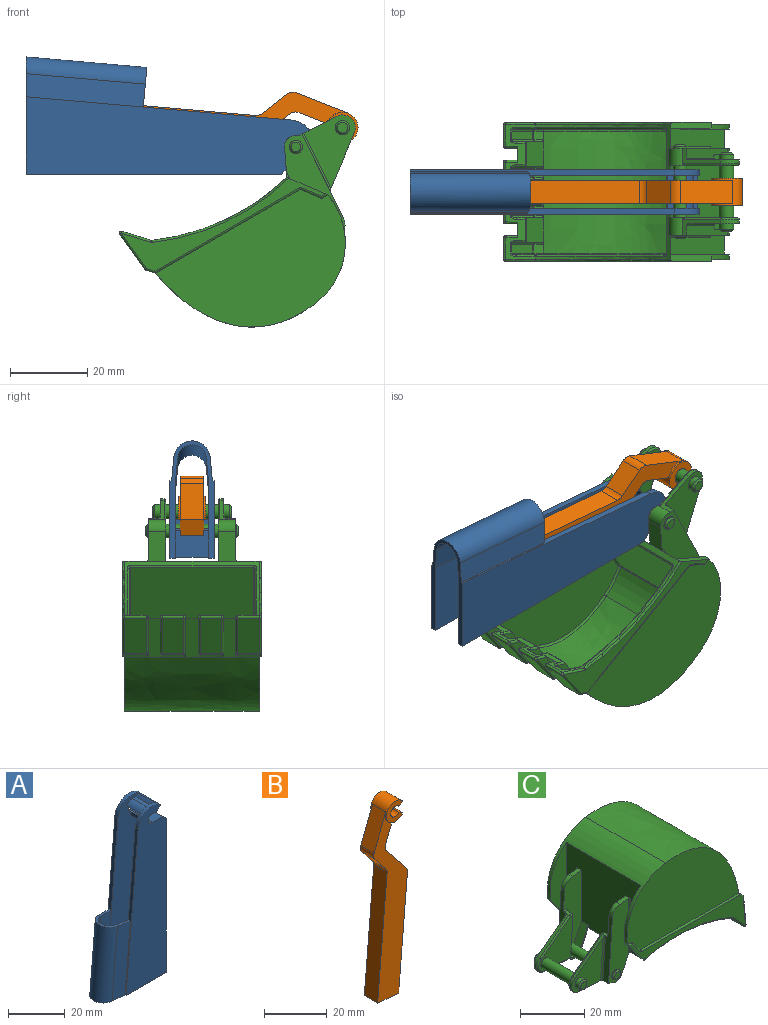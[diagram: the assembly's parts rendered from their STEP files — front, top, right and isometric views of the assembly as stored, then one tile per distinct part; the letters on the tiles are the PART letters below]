
ASSEMBLY  parts=3 mates=3
PART A: 29 faces, bbox 30.3x11.5x75.4 mm
  f0: plane 68.6x6mm, normal (-1,0,0.09), area 72.7mm2, adj f5,f6,f12,f14,f22,f25
  f1: plane 68.6x6mm, normal (-1,0,0.09), area 72.7mm2, adj f6,f12,f13,f19,f22,f24
  f2: cylinder r=1.9mm len=11.5mm, axis (0,1,0), area 30.8mm2, adj f5,f9,f10,f13,f14,f19,f20,f21
  f3: cylinder r=3.4mm len=8.5mm, axis (0,1,0), area 29.8mm2, adj f14,f17,f19,f20
  f4: plane 66.22x1.5mm, normal (1,0,0), area 99.3mm2, adj f5,f6,f8,f14
  f5: plane 75x20mm, normal (0,-1,0), area 1199.2mm2, adj f0,f2,f4,f6,f8,f9,f10,f11
  f6: plane 30.33x11.5mm, normal (0,0,-1), area 84.6mm2, adj f0,f1,f4,f5,f7,f13,f14,f19
  f7: plane 66.22x1.5mm, normal (1,0,0), area 99.3mm2, adj f6,f8,f13,f19
  f8: plane 11.5x1.77mm, normal (0.71,0,0.71), area 25.5mm2, adj f4,f5,f7,f9,f13,f14,f15,f19
  f9: plane 11.5x5.25mm, normal (0,0,1), area 60.3mm2, adj f2,f5,f8,f13
  f10: plane 11.5x2.5mm, normal (0,0,-1), area 28.7mm2, adj f2,f5,f11,f13
  f11: plane 11.5x1.77mm, normal (0.71,0,-0.71), area 28.8mm2, adj f5,f10,f12,f13
  f12: cylinder r=7.01mm len=11.5mm, axis (0,1,0), area 58.1mm2, adj f0,f1,f5,f11,f13,f14,f18,f19
  f13: plane 75x20mm, normal (0,1,0), area 1199.2mm2, adj f1,f2,f6,f7,f8,f9,f10,f11
  f14: plane 75x20mm, normal (0,1,0), area 1179.4mm2, adj f0,f2,f3,f4,f6,f8,f12,f15
  f15: plane 8.5x6.75mm, normal (0,0,-1), area 57.3mm2, adj f8,f14,f16,f19
  f16: cylinder r=3.4mm len=8.5mm, axis (0,1,0), area 6.3mm2, adj f14,f15,f19,f21
  f17: plane 8.5x1.88mm, normal (0,0,1), area 15.9mm2, adj f3,f14,f18,f19
  f18: plane 8.5x1.07mm, normal (-0.71,0,0.71), area 12.8mm2, adj f12,f14,f17,f19
  f19: plane 75x20mm, normal (0,-1,0), area 1179.4mm2, adj f1,f2,f3,f6,f7,f8,f12,f15
  f20: plane 8.5x2.18mm, normal (0,0,-1), area 18.5mm2, adj f2,f3,f14,f19
  f21: plane 8.5x1.57mm, normal (-1,0,0), area 13.3mm2, adj f2,f14,f16,f19
  f22: plane 10.51x10.25mm, normal (0.09,0,1), area 24.5mm2, adj f0,f1,f23,f24,f25,f26,f27,f28
  f23: plane 30.9x8.55mm, normal (0.09,-1,-0.01), area 181.2mm2, adj f6,f19,f22,f27
  f24: plane 30.91x8.64mm, normal (-0.09,1,0.01), area 183.9mm2, adj f1,f6,f22,f28
  f25: plane 30.91x8.64mm, normal (-0.09,-1,0.01), area 183.9mm2, adj f0,f6,f22,f28
  f26: plane 30.9x8.55mm, normal (0.09,1,-0.01), area 181.2mm2, adj f6,f14,f22,f27
  f27: cylinder r=3.75mm len=31.5mm, axis (-0.09,0,-1), area 347.3mm2, adj f6,f22,f23,f26
  f28: cylinder r=4.75mm len=31.67mm, axis (-0.09,0,-1), area 440.8mm2, adj f6,f22,f24,f25
PART B: 18 faces, bbox 15.3x7x76.2 mm
  f0: plane 13.5x6mm, normal (-0.93,0,0.37), area 87mm2, adj f7,f8,f11,f15
  f1: plane 6.25x6mm, normal (-0.78,0,-0.62), area 47.9mm2, adj f7,f8,f15,f16
  f2: plane 48.82x6mm, normal (-1,0,0.09), area 294mm2, adj f3,f7,f8,f16
  f3: plane 9.46x6mm, normal (-0.09,0,-1), area 57mm2, adj f2,f4,f7,f8
  f4: plane 46.35x6mm, normal (1,0,-0.09), area 279.2mm2, adj f3,f5,f7,f8
  f5: plane 12.08x9.62mm, normal (0.78,0,0.62), area 92.7mm2, adj f4,f7,f8,f17
  f6: plane 7.39x6mm, normal (0.93,0,-0.37), area 47.6mm2, adj f7,f8,f11,f17
  f7: plane 73.64x15.3mm, normal (0,-1,0), area 571.5mm2, adj f0,f1,f2,f3,f4,f5,f6,f11
  f8: plane 73.64x15.3mm, normal (0,1,0), area 571.5mm2, adj f0,f1,f2,f3,f4,f5,f6,f11
  f9: cylinder r=1.98mm len=7mm, axis (0,1,0), area 70.9mm2, adj f10,f12,f13,f14
  f10: plane 7x1.7mm, normal (0.54,0,-0.84), area 14.2mm2, adj f9,f11,f13,f14
  f11: cylinder r=4mm len=8mm, axis (0,1,0), area 103mm2, adj f0,f6,f7,f8,f10,f12,f13,f14
  f12: plane 7x1.7mm, normal (0.54,0,0.84), area 14.2mm2, adj f9,f11,f13,f14
  f13: plane 8x7.35mm, normal (0,-1,0), area 31mm2, adj f9,f10,f11,f12
  f14: plane 8x7.35mm, normal (0,1,0), area 31mm2, adj f9,f10,f11,f12
  f15: cylinder r=2.5mm len=6mm, axis (0,1,0), area 15.7mm2, adj f0,f1,f7,f8
  f16: cylinder r=2.5mm len=6mm, axis (0,-1,0), area 11.4mm2, adj f1,f2,f7,f8
  f17: cylinder r=2.5mm len=6mm, axis (0,-1,0), area 15.7mm2, adj f5,f6,f7,f8
PART C: 247 faces, bbox 67.8x36.4x43.8 mm
  f0: plane 24.35x2.5mm, normal (-1,0,0.07), area 53.1mm2, adj f55,f57,f64,f228,f232,f241,f245
  f1: plane 4.04x2.02mm, normal (-0.09,0,1), area 6.1mm2, adj f3,f10,f65,f221,f243
  f2: plane 24.35x2.5mm, normal (-1,0,0.07), area 53.1mm2, adj f3,f65,f71,f221,f222,f242,f244
  f3: cylinder r=3.71mm len=3.44mm, axis (0,-1,0), area 7.8mm2, adj f1,f2,f65,f221
  f4: plane 21.74x16.7mm, normal (0,-1,0), area 138.3mm2, adj f10,f66,f67,f72,f212,f223,f224,f225
  f5: plane 40.11x36.93mm, normal (0,-1,0), area 942.8mm2, adj f108,f109,f117,f126,f127,f136,f142,f143
  f6: plane 50.92x17.64mm, normal (0,1,0), area 173.3mm2, adj f30,f79,f81,f82,f84,f90,f99,f111
  f7: cylinder r=19.62mm len=35mm, axis (0,1,0), area 423.3mm2, adj f8,f10,f11,f12,f13,f30,f77,f78
  f8: extruded ~35x32.21mm, area 1668.8mm2, adj f7,f15,f16,f17,f31,f47,f50,f51
  f9: plane 50.92x17.64mm, normal (0,-1,0), area 173.3mm2, adj f13,f91,f100,f105,f113,f129,f144,f155
  f10: plane 32.6x27.74mm, normal (-1,0,0), area 815.5mm2, adj f1,f4,f7,f11,f12,f29,f56,f59
  f11: plane 27.74x7.24mm, normal (0,1,0), area 132.3mm2, adj f7,f10,f13
  f12: plane 27.74x7.24mm, normal (0,-1,0), area 132.3mm2, adj f7,f10,f30
  f13: plane 9.4x7.13mm, normal (-0.8,0,-0.6), area 19.6mm2, adj f7,f9,f11,f29,f91,f155
  f14: cylinder r=17.92mm len=31.6mm, axis (0,1,0), area 270.4mm2, adj f34,f126,f141,f152
  f15: plane 5.64x1.85mm, normal (0.73,0,0.69), area 14.3mm2, adj f8,f77,f114,f129,f130
  f16: plane 5.64x1.85mm, normal (0.73,0,0.69), area 14.3mm2, adj f8,f78,f83,f89,f90
  f17: plane 5.64x1.85mm, normal (0.73,0,0.69), area 14.3mm2, adj f8,f193,f197,f199
  f18: plane 11.17x5.64mm, normal (1,0,0.09), area 63.2mm2, adj f88,f89,f98,f99
  f19: plane 11.17x5.64mm, normal (1,0,0.09), area 63.2mm2, adj f191,f192,f196,f197
  f20: plane 11.17x5.64mm, normal (1,0,0.09), area 63.2mm2, adj f203,f204,f208,f209
  f21: plane 11.17x5.64mm, normal (1,0,0.09), area 63.2mm2, adj f130,f131,f144,f145
  f22: plane 35x5.81mm, normal (-0.73,0,-0.68), area 82mm2, adj f47,f50,f51,f87,f98,f103,f106,f110
  f23: plane 9.67x2.24mm, normal (-1,0,-0.09), area 21.7mm2, adj f176,f177,f183,f184
  f24: plane 2.24x1.8mm, normal (-0.73,0,-0.69), area 5.5mm2, adj f34,f166,f175,f176
  f25: plane 9.67x2.24mm, normal (-1,0,-0.09), area 21.7mm2, adj f96,f101,f109,f110
  f26: plane 9.67x2.24mm, normal (-1,0,-0.09), area 21.7mm2, adj f123,f124,f139,f140
  f27: plane 2.24x1.8mm, normal (-0.73,0,-0.69), area 5.5mm2, adj f34,f107,f124,f125
  f28: plane 2.24x1.8mm, normal (-0.73,0,-0.69), area 5.5mm2, adj f34,f92,f96,f108
  f29: cylinder r=59.35mm len=38.42mm, axis (0,1,0), area 105mm2, adj f10,f13,f30,f58,f66,f112,f128,f143
  f30: plane 9.4x7.13mm, normal (-0.8,0,-0.6), area 19.6mm2, adj f6,f7,f12,f29,f79,f112
  f31: plane 5.64x1.85mm, normal (0.73,0,0.69), area 14.3mm2, adj f8,f205,f209,f211
  f32: plane 9.67x2.24mm, normal (-1,0,-0.09), area 21.7mm2, adj f163,f164,f173,f174
  f33: plane 2.24x1.8mm, normal (-0.73,0,-0.69), area 5.5mm2, adj f34,f151,f164,f165
  f34: extruded ~31.6x30.39mm, area 1440.4mm2, adj f14,f24,f27,f28,f33,f36,f41,f43
  f35: plane 40.11x36.93mm, normal (0,1,0), area 942.8mm2, adj f152,f153,f159,f166,f167,f172,f177,f178
  f36: plane 8.97x7.88mm, normal (-1,0,0), area 58.4mm2, adj f34,f37,f38,f125,f150,f151,f157,f162
  f37: plane 9.78x2.13mm, normal (0,-1,0), area 13mm2, adj f36,f151,f162,f163
  f38: plane 9.78x2.13mm, normal (0,1,0), area 13mm2, adj f36,f125,f140,f150
  f39: plane 9.78x2.13mm, normal (0,-1,0), area 13mm2, adj f41,f107,f122,f123
  f40: plane 9.78x2.13mm, normal (0,1,0), area 13mm2, adj f41,f92,f101,f106
  f41: plane 8.97x7.72mm, normal (-1,0,0), area 57mm2, adj f34,f39,f40,f92,f106,f107,f115,f122
  f42: plane 9.78x2.13mm, normal (0,1,0), area 13mm2, adj f43,f165,f174,f182
  f43: plane 8.97x7.72mm, normal (-1,0,0), area 57mm2, adj f34,f42,f44,f165,f175,f182,f185,f187
  f44: plane 9.78x2.13mm, normal (0,-1,0), area 13mm2, adj f43,f175,f183,f187
  f45: plane 12.63x2.45mm, normal (0,1,0), area 19.2mm2, adj f47,f114,f131,f132
  f46: plane 12.63x2.45mm, normal (0,-1,0), area 19.2mm2, adj f47,f200,f204,f205
  f47: plane 11.68x4.33mm, normal (1,0,0), area 35.8mm2, adj f8,f22,f45,f46,f114,f132,f200,f205
  f48: plane 12.63x2.45mm, normal (0,1,0), area 19.2mm2, adj f50,f202,f208,f211
  f49: plane 12.63x2.45mm, normal (0,-1,0), area 19.2mm2, adj f50,f188,f192,f193
  f50: plane 11.68x4.49mm, normal (1,0,0), area 37.7mm2, adj f8,f22,f48,f49,f188,f193,f202,f211
  f51: plane 11.68x4.33mm, normal (1,0,0), area 35.8mm2, adj f8,f22,f52,f53,f83,f87,f190,f199
  f52: plane 12.63x2.45mm, normal (0,1,0), area 19.2mm2, adj f51,f190,f196,f199
  f53: plane 12.63x2.45mm, normal (0,-1,0), area 19.2mm2, adj f51,f83,f87,f88
  f54: plane 31.6x25.9mm, normal (1,0,0), area 818.6mm2, adj f141,f142,f153,f154
  f55: plane 28.98x8.56mm, normal (0,-1,0), area 191.3mm2, adj f0,f56,f57,f58,f60,f64,f75,f246
  f56: plane 4.04x2.02mm, normal (-0.09,0,1), area 6.1mm2, adj f10,f55,f57,f232,f246
  f57: cylinder r=3.71mm len=3.44mm, axis (0,1,0), area 7.8mm2, adj f0,f55,f56,f232
  f58: plane 7.35x5.44mm, normal (0.9,0,-0.43), area 34.6mm2, adj f29,f55,f59,f60,f246
  f59: plane 21.74x16.7mm, normal (0,1,0), area 138.3mm2, adj f10,f58,f60,f72,f212,f227,f229,f230
  f60: cylinder r=2.94mm len=5.1mm, axis (0,1,0), area 25mm2, adj f55,f58,f59,f64,f240
  f61: plane 15.93x13.79mm, normal (0,-1,0), area 120.8mm2, adj f62,f63,f64,f215,f245
  f62: plane 13.2x10.11mm, normal (-0.61,0,0.8), area 16.4mm2, adj f61,f63,f228,f238,f245
  f63: cylinder r=3.31mm len=5.93mm, axis (0,1,0), area 8.1mm2, adj f61,f62,f64,f239
  f64: plane 11.12x4mm, normal (-0.05,0,-1), area 14.4mm2, adj f0,f55,f60,f61,f63,f240,f245
  f65: plane 28.98x8.56mm, normal (0,1,0), area 191.3mm2, adj f1,f2,f3,f66,f67,f71,f74,f243
  f66: plane 7.35x5.44mm, normal (0.9,0,-0.43), area 34.6mm2, adj f4,f29,f65,f67,f243
  f67: cylinder r=2.94mm len=5.1mm, axis (0,-1,0), area 25mm2, adj f4,f65,f66,f71,f233
  f68: plane 15.93x13.79mm, normal (0,1,0), area 120.8mm2, adj f69,f70,f71,f214,f244
  f69: plane 13.2x10.11mm, normal (-0.61,0,0.8), area 16.4mm2, adj f68,f70,f222,f236,f244
  f70: cylinder r=3.31mm len=5.93mm, axis (0,-1,0), area 8.1mm2, adj f68,f69,f71,f235
  f71: plane 11.12x4mm, normal (-0.05,0,-1), area 14.4mm2, adj f2,f65,f67,f68,f70,f233,f244
  f72: cylinder r=1.75mm len=19.5mm, axis (0,1,0), area 208.2mm2, adj f4,f59,f221,f223,f225,f229,f230,f232
  f73: plane 2.5x2.5mm, normal (0,1,0), area 4.9mm2, adj f219
  f74: cylinder r=1.75mm len=3.5mm, axis (0,1,0), area 4.4mm2, adj f65,f219
  f75: cylinder r=1.75mm len=3.5mm, axis (0,1,0), area 4.4mm2, adj f55,f220
  f76: plane 2.5x2.5mm, normal (0,-1,0), area 4.9mm2, adj f220
  f77: plane 49.26x30.07mm, normal (0,-1,0), area 1081.4mm2, adj f7,f8,f15,f91,f97,f100,f105,f113
  f78: plane 49.26x30.07mm, normal (0,1,0), area 1081.4mm2, adj f7,f8,f16,f79,f80,f81,f82,f84
  f79: cylinder r=0.5mm len=1.63mm, axis (-1,0,0), area 1.1mm2, adj f6,f30,f78,f80
  f80: sphere r=0.5mm, area 0.3mm2, adj f78,f79,f81
  f81: cylinder r=0.5mm len=4.68mm, axis (-0.6,0,0.8), area 4.3mm2, adj f6,f78,f80,f82
  f82: torus R=1mm, axis (0,-1,0), area 0.5mm2, adj f6,f78,f81,f84
  f83: cylinder r=0.5mm len=2.19mm, axis (-0.69,0,0.73), area 1.8mm2, adj f16,f51,f53,f85
  f84: cylinder r=0.5mm len=42.9mm, axis (-1,0,0), area 33.7mm2, adj f6,f78,f82,f86
  f85: sphere r=0.5mm, area 0.2mm2, adj f83,f88,f89
  f86: sphere r=0.5mm, area 0.3mm2, adj f78,f84,f90
  f87: cylinder r=0.5mm len=2.98mm, axis (0.68,0,-0.73), area 2.6mm2, adj f22,f51,f53,f93
  f88: cylinder r=0.5mm len=11.21mm, axis (-0.09,0,1), area 8.8mm2, adj f18,f53,f85,f93
  f89: cylinder r=0.5mm len=5.64mm, axis (0,1,0), area 1.9mm2, adj f16,f18,f85,f94
  f90: cylinder r=0.5mm len=2.05mm, axis (-0.69,0,0.73), area 1.8mm2, adj f6,f16,f86,f94
  f91: cylinder r=0.5mm len=1.63mm, axis (-1,0,0), area 1.1mm2, adj f9,f13,f77,f97
  f92: cylinder r=0.5mm len=2.14mm, axis (0.69,0,-0.73), area 1.7mm2, adj f28,f40,f41,f95
  f93: sphere r=0.5mm, area 0.7mm2, adj f87,f88,f98
  f94: sphere r=0.5mm, area 0.1mm2, adj f89,f90,f99
  f95: sphere r=0.5mm, area 0.2mm2, adj f92,f96,f101
  f96: cylinder r=0.5mm len=2.24mm, axis (0,-1,0), area 0.7mm2, adj f25,f28,f95,f102
  f97: sphere r=0.5mm, area 0.2mm2, adj f77,f91,f100
  f98: cylinder r=0.5mm len=5.64mm, axis (0,1,0), area 7mm2, adj f18,f22,f93,f104
  f99: cylinder r=0.5mm len=11.21mm, axis (-0.09,0,1), area 8.8mm2, adj f6,f18,f94,f104
  f100: cylinder r=0.5mm len=4.68mm, axis (-0.6,0,0.8), area 4.3mm2, adj f9,f77,f97,f105
  f101: cylinder r=0.5mm len=9.72mm, axis (0.09,0,-1), area 7.1mm2, adj f25,f40,f95,f103
  f102: sphere r=0.5mm, area 0.1mm2, adj f96,f108,f109
  f103: bspline ~1.55x1.12mm, area 1mm2, adj f22,f101,f106,f110
  f104: sphere r=0.5mm, area 0.7mm2, adj f98,f99,f111
  f105: torus R=1mm, axis (0,-1,0), area 0.5mm2, adj f9,f77,f100,f113
  f106: cylinder r=0.5mm len=2.64mm, axis (-0.68,0,0.73), area 2.2mm2, adj f22,f40,f41,f103,f115
  f107: cylinder r=0.5mm len=2.14mm, axis (-0.69,0,0.73), area 1.7mm2, adj f27,f39,f41,f116
  f108: cylinder r=0.5mm len=2.25mm, axis (0.69,0,-0.73), area 2mm2, adj f5,f28,f102,f117
  f109: cylinder r=0.5mm len=9.72mm, axis (0.09,0,-1), area 7.1mm2, adj f5,f25,f102,f118
  f110: cylinder r=0.5mm len=2.24mm, axis (0,-1,0), area 0.7mm2, adj f22,f25,f103,f118
  f111: cylinder r=0.5mm len=6.15mm, axis (0.68,0,-0.73), area 6.2mm2, adj f6,f22,f104,f119
  f112: torus R=59.85mm, axis (0,-1,0), area 31mm2, adj f6,f29,f30,f119
  f113: cylinder r=0.5mm len=42.9mm, axis (-1,0,0), area 33.7mm2, adj f9,f77,f105,f120
  f114: cylinder r=0.5mm len=2.19mm, axis (-0.69,0,0.73), area 1.8mm2, adj f15,f45,f47,f121
  f115: cylinder r=0.5mm len=6.18mm, axis (0,-1,0), area 2.2mm2, adj f22,f41,f106,f122
  f116: sphere r=0.5mm, area 0.1mm2, adj f107,f123,f124
  f117: bspline ~45.86x28.35mm, area 35.6mm2, adj f5,f34,f108,f126
  f118: bspline ~1.77x1.31mm, area 1mm2, adj f22,f109,f110,f127
  f119: torus R=1mm, axis (0,-1,0), area 0.2mm2, adj f6,f111,f112,f128
  f120: sphere r=0.5mm, area 0.2mm2, adj f77,f113,f129
  f121: sphere r=0.5mm, area 0.1mm2, adj f114,f130,f131
  f122: cylinder r=0.5mm len=2.64mm, axis (0.68,0,-0.73), area 2.2mm2, adj f22,f39,f41,f115,f133
  f123: cylinder r=0.5mm len=9.72mm, axis (-0.09,0,1), area 7.1mm2, adj f26,f39,f116,f133
  f124: cylinder r=0.5mm len=2.24mm, axis (0,-1,0), area 0.7mm2, adj f26,f27,f116,f134
  f125: cylinder r=0.5mm len=2.14mm, axis (0.69,0,-0.73), area 1.7mm2, adj f27,f36,f38,f134
  f126: torus R=17.42mm, axis (0,-1,0), area 6.7mm2, adj f5,f14,f117,f135
  f127: cylinder r=0.5mm len=4.09mm, axis (-0.68,0,0.73), area 4mm2, adj f5,f22,f118,f136
  f128: cylinder r=0.5mm len=0.7mm, axis (0,1,0), area 0.1mm2, adj f22,f29,f119,f136
  f129: cylinder r=0.5mm len=2.05mm, axis (0.69,0,-0.73), area 1.8mm2, adj f9,f15,f120,f137
  f130: cylinder r=0.5mm len=5.64mm, axis (0,1,0), area 1.9mm2, adj f15,f21,f121,f137
  f131: cylinder r=0.5mm len=11.21mm, axis (0.09,0,-1), area 8.8mm2, adj f21,f45,f121,f138
  f132: cylinder r=0.5mm len=2.98mm, axis (-0.68,0,0.73), area 2.6mm2, adj f22,f45,f47,f138
  f133: bspline ~1.77x1.31mm, area 1mm2, adj f22,f122,f123,f139
  f134: sphere r=0.5mm, area 0.2mm2, adj f124,f125,f140
  f135: sphere r=0.5mm, area 0.2mm2, adj f126,f141,f142
  f136: torus R=1mm, axis (0,-1,0), area 0.2mm2, adj f5,f127,f128,f143
  f137: sphere r=0.5mm, area 0.2mm2, adj f129,f130,f144
  f138: sphere r=0.5mm, area 0.7mm2, adj f131,f132,f145
  f139: cylinder r=0.5mm len=2.24mm, axis (0,-1,0), area 0.7mm2, adj f22,f26,f133,f146
  f140: cylinder r=0.5mm len=9.72mm, axis (0.09,0,-1), area 7.1mm2, adj f26,f38,f134,f146
  f141: cylinder r=0.5mm len=31.6mm, axis (0,1,0), area 15.1mm2, adj f14,f54,f135,f147
  f142: cylinder r=0.5mm len=25.9mm, axis (0,0,-1), area 20.3mm2, adj f5,f54,f135,f148
  f143: torus R=59.85mm, axis (0,-1,0), area 29mm2, adj f5,f29,f136,f148
  f144: cylinder r=0.5mm len=11.21mm, axis (0.09,0,-1), area 8.8mm2, adj f9,f21,f137,f149
  f145: cylinder r=0.5mm len=5.64mm, axis (0,1,0), area 7mm2, adj f21,f22,f138,f149
  f146: bspline ~1.55x1.12mm, area 1mm2, adj f22,f139,f140,f150
  f147: sphere r=0.5mm, area 0.2mm2, adj f141,f152,f153
  f148: bspline ~1.22x1.19mm, area 0.8mm2, adj f29,f142,f143,f154
  f149: sphere r=0.5mm, area 0.7mm2, adj f144,f145,f156
  f150: cylinder r=0.5mm len=2.64mm, axis (-0.68,0,0.73), area 2.2mm2, adj f22,f36,f38,f146,f157
  f151: cylinder r=0.5mm len=2.14mm, axis (-0.69,0,0.73), area 1.7mm2, adj f33,f36,f37,f158
  f152: torus R=17.42mm, axis (0,-1,0), area 6.7mm2, adj f14,f35,f147,f159
  f153: cylinder r=0.5mm len=25.9mm, axis (0,0,1), area 20.3mm2, adj f35,f54,f147,f160
  f154: cylinder r=0.5mm len=31.6mm, axis (0,1,0), area 21.3mm2, adj f29,f54,f148,f160
  f155: torus R=59.85mm, axis (0,-1,0), area 31mm2, adj f9,f13,f29,f161
  f156: cylinder r=0.5mm len=6.15mm, axis (-0.68,0,0.73), area 6.2mm2, adj f9,f22,f149,f161
  f157: cylinder r=0.5mm len=6.34mm, axis (0,-1,0), area 2.2mm2, adj f22,f36,f150,f162
  f158: sphere r=0.5mm, area 0.1mm2, adj f151,f163,f164
  f159: bspline ~45.86x28.35mm, area 35.6mm2, adj f34,f35,f152,f166
  f160: bspline ~1.22x1.15mm, area 0.8mm2, adj f29,f153,f154,f167
  f161: torus R=1mm, axis (0,-1,0), area 0.2mm2, adj f9,f155,f156,f168
  f162: cylinder r=0.5mm len=2.64mm, axis (0.68,0,-0.73), area 2.2mm2, adj f22,f36,f37,f157,f169
  f163: cylinder r=0.5mm len=9.72mm, axis (-0.09,0,1), area 7.1mm2, adj f32,f37,f158,f169
  f164: cylinder r=0.5mm len=2.24mm, axis (0,-1,0), area 0.7mm2, adj f32,f33,f158,f170
  f165: cylinder r=0.5mm len=2.14mm, axis (0.69,0,-0.73), area 1.7mm2, adj f33,f42,f43,f170
  f166: cylinder r=0.5mm len=2.25mm, axis (-0.69,0,0.73), area 2mm2, adj f24,f35,f159,f171
  f167: torus R=59.85mm, axis (0,-1,0), area 29mm2, adj f29,f35,f160,f172
  f168: cylinder r=0.5mm len=0.7mm, axis (0,1,0), area 0.1mm2, adj f22,f29,f161,f172
  f169: bspline ~1.77x1.31mm, area 1mm2, adj f22,f162,f163,f173
  f170: sphere r=0.5mm, area 0.2mm2, adj f164,f165,f174
  f171: sphere r=0.5mm, area 0.2mm2, adj f166,f176,f177
  f172: torus R=1mm, axis (0,-1,0), area 0.2mm2, adj f35,f167,f168,f178
  f173: cylinder r=0.5mm len=2.24mm, axis (0,-1,0), area 0.7mm2, adj f22,f32,f169,f179
  f174: cylinder r=0.5mm len=9.72mm, axis (0.09,0,-1), area 7.1mm2, adj f32,f42,f170,f179
  f175: cylinder r=0.5mm len=2.14mm, axis (-0.69,0,0.73), area 1.7mm2, adj f24,f43,f44,f180
  f176: cylinder r=0.5mm len=2.24mm, axis (0,-1,0), area 0.7mm2, adj f23,f24,f171,f180
  f177: cylinder r=0.5mm len=9.72mm, axis (-0.09,0,1), area 7.1mm2, adj f23,f35,f171,f181
  f178: cylinder r=0.5mm len=4.09mm, axis (0.68,0,-0.73), area 4mm2, adj f22,f35,f172,f181
  f179: bspline ~1.55x1.12mm, area 1mm2, adj f22,f173,f174,f182
  f180: sphere r=0.5mm, area 0.1mm2, adj f175,f176,f183
  f181: bspline ~1.77x1.31mm, area 1mm2, adj f22,f177,f178,f184
  f182: cylinder r=0.5mm len=2.64mm, axis (-0.68,0,0.73), area 2.2mm2, adj f22,f42,f43,f179,f185
  f183: cylinder r=0.5mm len=9.72mm, axis (-0.09,0,1), area 7.1mm2, adj f23,f44,f180,f186
  f184: cylinder r=0.5mm len=2.24mm, axis (0,-1,0), area 0.7mm2, adj f22,f23,f181,f186
  f185: cylinder r=0.5mm len=6.18mm, axis (0,-1,0), area 2.2mm2, adj f22,f43,f182,f187
  f186: bspline ~1.77x1.31mm, area 1mm2, adj f22,f183,f184,f187
  f187: cylinder r=0.5mm len=2.64mm, axis (0.68,0,-0.73), area 2.2mm2, adj f22,f43,f44,f185,f186
  f188: cylinder r=0.5mm len=2.98mm, axis (0.68,0,-0.73), area 2.6mm2, adj f22,f49,f50,f189
  f189: sphere r=0.5mm, area 0.7mm2, adj f188,f191,f192
  f190: cylinder r=0.5mm len=2.98mm, axis (-0.68,0,0.73), area 2.6mm2, adj f22,f51,f52,f194
  f191: cylinder r=0.5mm len=5.64mm, axis (0,1,0), area 7mm2, adj f19,f22,f189,f194
  f192: cylinder r=0.5mm len=11.21mm, axis (-0.09,0,1), area 8.8mm2, adj f19,f49,f189,f195
  f193: cylinder r=0.5mm len=2.19mm, axis (-0.69,0,0.73), area 1.8mm2, adj f17,f49,f50,f195
  f194: sphere r=0.5mm, area 0.7mm2, adj f190,f191,f196
  f195: sphere r=0.5mm, area 0.2mm2, adj f192,f193,f197
  f196: cylinder r=0.5mm len=11.21mm, axis (0.09,0,-1), area 8.8mm2, adj f19,f52,f194,f198
  f197: cylinder r=0.5mm len=5.64mm, axis (0,1,0), area 1.9mm2, adj f17,f19,f195,f198
  f198: sphere r=0.5mm, area 0.1mm2, adj f196,f197,f199
  f199: cylinder r=0.5mm len=2.19mm, axis (-0.69,0,0.73), area 1.8mm2, adj f17,f51,f52,f198
  f200: cylinder r=0.5mm len=2.98mm, axis (0.68,0,-0.73), area 2.6mm2, adj f22,f46,f47,f201
  f201: sphere r=0.5mm, area 0.7mm2, adj f200,f203,f204
  f202: cylinder r=0.5mm len=2.98mm, axis (-0.68,0,0.73), area 2.6mm2, adj f22,f48,f50,f206
  f203: cylinder r=0.5mm len=5.64mm, axis (0,1,0), area 7mm2, adj f20,f22,f201,f206
  f204: cylinder r=0.5mm len=11.21mm, axis (-0.09,0,1), area 8.8mm2, adj f20,f46,f201,f207
  f205: cylinder r=0.5mm len=2.19mm, axis (-0.69,0,0.73), area 1.8mm2, adj f31,f46,f47,f207
  f206: sphere r=0.5mm, area 0.7mm2, adj f202,f203,f208
  f207: sphere r=0.5mm, area 0.2mm2, adj f204,f205,f209
  f208: cylinder r=0.5mm len=11.21mm, axis (0.09,0,-1), area 8.8mm2, adj f20,f48,f206,f210
  f209: cylinder r=0.5mm len=5.64mm, axis (0,1,0), area 1.9mm2, adj f20,f31,f207,f210
  f210: sphere r=0.5mm, area 0.1mm2, adj f208,f209,f211
  f211: cylinder r=0.5mm len=2.19mm, axis (-0.69,0,0.73), area 1.8mm2, adj f31,f48,f50,f210
  f212: cylinder r=1.88mm len=13.5mm, axis (0,1,0), area 159mm2, adj f4,f59
  f213: plane 2.75x2.75mm, normal (0,1,0), area 5.9mm2, adj f218
  f214: cylinder r=1.88mm len=3.75mm, axis (0,1,0), area 17.7mm2, adj f68,f218
  f215: cylinder r=1.88mm len=3.75mm, axis (0,1,0), area 17.7mm2, adj f61,f217
  f216: plane 2.75x2.75mm, normal (0,-1,0), area 5.9mm2, adj f217
  f217: cone r=1.38mm half-angle=45deg, axis (0,1,0), area 7.2mm2, adj f215,f216
  f218: cone r=1.88mm half-angle=45deg, axis (0,-1,0), area 7.2mm2, adj f213,f214
  f219: cone r=1.75mm half-angle=45deg, axis (0,-1,0), area 6.7mm2, adj f73,f74
  f220: cone r=1.25mm half-angle=45deg, axis (0,1,0), area 6.7mm2, adj f75,f76
  f221: plane 28.52x7.89mm, normal (0,-1,0), area 173.9mm2, adj f1,f2,f3,f10,f72,f223,f224,f225
  f222: plane 2x1.26mm, normal (0.07,0,1), area 2.5mm2, adj f2,f69,f223,f234,f242
  f223: plane 14.06x3mm, normal (1,0,-0.07), area 40.8mm2, adj f4,f72,f221,f222,f234,f242
  f224: plane 7.85x3.78mm, normal (-0.9,0,0.43), area 26.1mm2, adj f4,f10,f221,f226
  f225: plane 3x1.26mm, normal (1,0,-0.07), area 3.8mm2, adj f4,f72,f221,f226
  f226: cylinder r=2.44mm len=3.99mm, axis (0,-1,0), area 14.2mm2, adj f4,f221,f224,f225
  f227: plane 7.85x3.78mm, normal (-0.9,0,0.43), area 26.1mm2, adj f10,f59,f231,f232
  f228: plane 2x1.26mm, normal (0.07,0,1), area 2.5mm2, adj f0,f62,f229,f237,f241
  f229: plane 14.06x3mm, normal (1,0,-0.07), area 40.8mm2, adj f59,f72,f228,f232,f237,f241
  f230: plane 3x1.26mm, normal (1,0,-0.07), area 3.8mm2, adj f59,f72,f231,f232
  f231: cylinder r=2.44mm len=3.99mm, axis (0,1,0), area 14.2mm2, adj f59,f227,f230,f232
  f232: plane 28.52x7.89mm, normal (0,1,0), area 173.9mm2, adj f0,f10,f56,f57,f72,f227,f229,f230
  f233: cylinder r=0.5mm len=11.14mm, axis (1,0,-0.05), area 8.6mm2, adj f4,f67,f71,f235
  f234: cylinder r=0.5mm len=1.29mm, axis (1,0,-0.07), area 0.9mm2, adj f4,f222,f223,f236
  f235: torus R=2.81mm, axis (0,1,0), area 6mm2, adj f4,f70,f233,f236
  f236: cylinder r=0.5mm len=13.32mm, axis (-0.8,0,-0.61), area 12.8mm2, adj f4,f69,f234,f235
  f237: cylinder r=0.5mm len=1.29mm, axis (1,0,-0.07), area 0.9mm2, adj f59,f228,f229,f238
  f238: cylinder r=0.5mm len=13.32mm, axis (-0.8,0,-0.61), area 12.8mm2, adj f59,f62,f237,f239
  f239: torus R=2.81mm, axis (0,-1,0), area 6mm2, adj f59,f63,f238,f240
  f240: cylinder r=0.5mm len=11.14mm, axis (1,0,-0.05), area 8.6mm2, adj f59,f60,f64,f239
  f241: cylinder r=0.5mm len=1.29mm, axis (1,0,-0.07), area 1mm2, adj f0,f228,f229,f232
  f242: cylinder r=0.5mm len=1.29mm, axis (-1,0,0.07), area 1mm2, adj f2,f221,f222,f223
  f243: cylinder r=0.5mm len=21.49mm, axis (0,0,1), area 16.4mm2, adj f1,f10,f65,f66
  f244: cylinder r=0.5mm len=16.41mm, axis (-0.07,0,-1), area 12.7mm2, adj f2,f68,f69,f71
  f245: cylinder r=0.5mm len=16.41mm, axis (-0.07,0,-1), area 12.7mm2, adj f0,f61,f62,f64
  f246: cylinder r=0.5mm len=21.49mm, axis (0,0,1), area 16.4mm2, adj f10,f55,f56,f58
PLACE A rot(axis=(0,1,0),90deg) t=(-22.27,-6.59,-3.12)mm fixed
PLACE B rot(axis=(0,1,0),90deg) t=(-11.9,-6.59,-11.09)mm
PLACE C rot(axis=(0,1,0),150deg) t=(-22.27,-6.59,-3.12)mm
MATE revolute A.f2 <-> C.f72  axis (0,1,0) through (-22.27,-6.59,-3.12)mm
MATE parallel B.f2 <-> A.f0  axis (0.09,0,1) through (-57.12,-6.59,7.16)mm
MATE revolute B.f9 <-> C.f63  axis (0,1,0) through (-10.18,-6.59,1.87)mm
